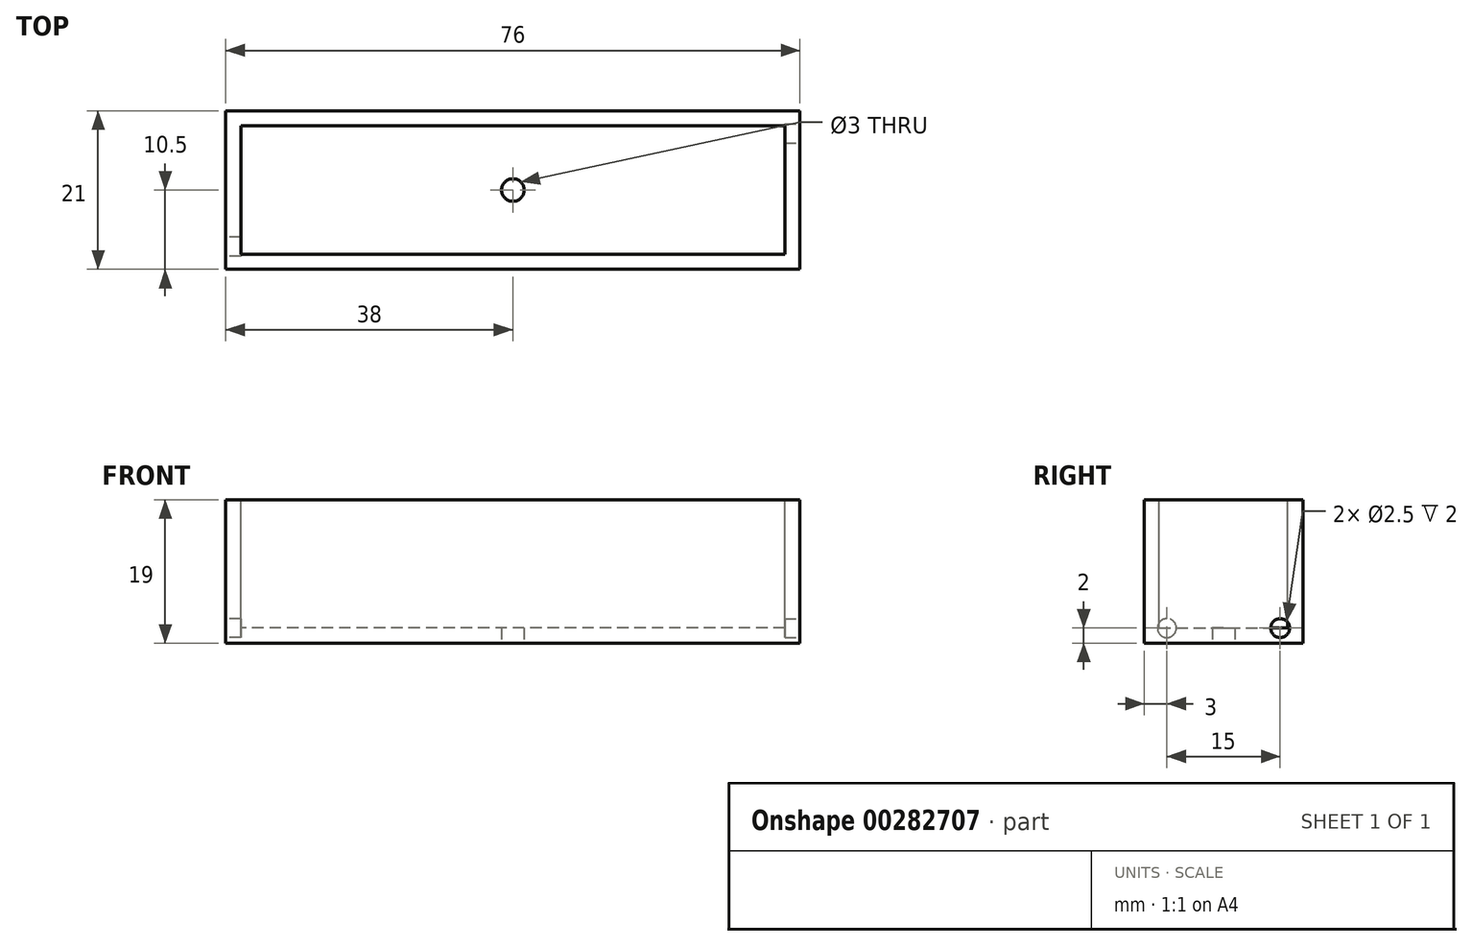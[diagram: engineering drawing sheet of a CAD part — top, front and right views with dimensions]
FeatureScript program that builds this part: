
annotation { "Feature Type Name" : "Feature", "Feature Type Description" : "" }
export const myFeature = defineFeature(function(context is Context, id is Id, definition is map)
    precondition{}
    {
        {
            var Q0;
            Q0=qCreatedBy(makeId("Top.planeOp"),FACE);
            var sketch = newSketch(context, id + "F0", { "sketchPlane" : qUnion([Q0])});
            skLineSegment(sketch, "E0.bottom", {"start": v(38, -10.5) * mm, "end": v(-38, -10.5) * mm});
            skLineSegment(sketch, "E0.top", {"start": v(38, 10.5) * mm, "end": v(-38, 10.5) * mm});
            skLineSegment(sketch, "E0.left", {"start": v(38, -10.5) * mm, "end": v(38, 10.5) * mm});
            skLineSegment(sketch, "E0.right", {"start": v(-38, -10.5) * mm, "end": v(-38, 10.5) * mm});
            skPoint(sketch, "E0.middle", {"position": v(0, 0) * mm});
            skSolve(sketch);
        }
        {
            var Q0;
            Q0=qSketchRegion(id+"F0",true);
            extrude(context, id + "F1", {"entities" : qUnion([Q0]), "depth" : 19 * mm});
        }
        {
            var Q0;
            Q0=makeQuery(id+"F1.opExtrude","CAP_FACE",FACE,{"disambiguationData":[OSD([sQuery(id+"F0.wireOp",EDGE,"E0.bottom"),sQuery(id+"F0.wireOp",EDGE,"E0.top"),sQuery(id+"F0.wireOp",EDGE,"E0.left"),sQuery(id+"F0.wireOp",EDGE,"E0.right")])],"isStart":false});
            var sketch = newSketch(context, id + "F2", { "sketchPlane" : qUnion([Q0])});
            skLineSegment(sketch, "E1.bottom", {"start": v(36, -8.5) * mm, "end": v(-36, -8.5) * mm});
            skLineSegment(sketch, "E1.top", {"start": v(36, 8.5) * mm, "end": v(-36, 8.5) * mm});
            skLineSegment(sketch, "E1.left", {"start": v(36, -8.5) * mm, "end": v(36, 8.5) * mm});
            skLineSegment(sketch, "E1.right", {"start": v(-36, -8.5) * mm, "end": v(-36, 8.5) * mm});
            skPoint(sketch, "E1.middle", {"position": v(0, 0) * mm});
            skSolve(sketch);
        }
        {
            var Q0;
            Q0=qSketchRegion(id+"F2",true);
            extrude(context, id + "F3", {"entities" : qUnion([Q0]), "operationType" : NewBodyOperationType.REMOVE, "oppositeDirection" : true, "depth" : 17 * mm});
        }
        {
            var Q0;
            Q0=makeQuery(id+"F1.opExtrude","CAP_FACE",FACE,{"disambiguationData":[OSD([sQuery(id+"F0.wireOp",EDGE,"E0.bottom"),sQuery(id+"F0.wireOp",EDGE,"E0.top"),sQuery(id+"F0.wireOp",EDGE,"E0.left"),sQuery(id+"F0.wireOp",EDGE,"E0.right")])],"isStart":true});
            var sketch = newSketch(context, id + "F4", { "sketchPlane" : qUnion([Q0])});
            skCircle(sketch, "E2", {"center": v(0, 0) * mm, "radius": 1.5 * mm});
            skSolve(sketch);
        }
        {
            var Q0;
            Q0=qSketchRegion(id+"F4",true);
            extrude(context, id + "F5", {"entities" : qUnion([Q0]), "operationType" : NewBodyOperationType.REMOVE, "endBound" : BoundingType.THROUGH_ALL, "oppositeDirection" : true, "depth" : 25 * mm});
        }
        {
            var Q0;
            Q0=makeQuery(id+"F1.opExtrude","SWEPT_FACE",FACE,{"disambiguationData":[OSD([sQuery(id+"F0.wireOp",EDGE,"E0.right")])]});
            var sketch = newSketch(context, id + "F6", { "sketchPlane" : qUnion([Q0])});
            skLineSegment(sketch, "E3.bottom", {"start": v(10.5, 0) * mm, "end": v(7.5, 0) * mm, "construction": true});
            skLineSegment(sketch, "E3.top", {"start": v(10.5, 2) * mm, "end": v(7.5, 2) * mm, "construction": true});
            skLineSegment(sketch, "E3.left", {"start": v(10.5, 0) * mm, "end": v(10.5, 2) * mm, "construction": true});
            skLineSegment(sketch, "E3.right", {"start": v(7.5, 0) * mm, "end": v(7.5, 2) * mm, "construction": true});
            skCircle(sketch, "E4", {"center": v(7.5, 2) * mm, "radius": 1.25 * mm});
            skPoint(sketch, "E5.centerSnap0", {"position": v(9, 0) * mm});
            skSolve(sketch);
        }
        {
            var Q0;
            Q0=qSketchRegion(id+"F6",true);
            extrude(context, id + "F7", {"entities" : qUnion([Q0]), "operationType" : NewBodyOperationType.REMOVE, "oppositeDirection" : true, "depth" : 2 * mm});
        }
        {
            var Q0;
            Q0=makeQuery(id+"F1.opExtrude","SWEPT_FACE",FACE,{"disambiguationData":[OSD([sQuery(id+"F0.wireOp",EDGE,"E0.left")])]});
            var sketch = newSketch(context, id + "F8", { "sketchPlane" : qUnion([Q0])});
            skLineSegment(sketch, "E6.bottom", {"start": v(10.5, 0) * mm, "end": v(7.5, 0) * mm, "construction": true});
            skLineSegment(sketch, "E6.top", {"start": v(10.5, 2) * mm, "end": v(7.5, 2) * mm});
            skLineSegment(sketch, "E6.left", {"start": v(10.5, 0) * mm, "end": v(10.5, 2) * mm, "construction": true});
            skLineSegment(sketch, "E6.right", {"start": v(7.5, 0) * mm, "end": v(7.5, 2) * mm});
            skCircle(sketch, "E7", {"center": v(7.5, 2) * mm, "radius": 1.25 * mm});
            skSolve(sketch);
        }
        {
            var Q0;
            Q0=qSketchRegion(id+"F8",true);
            extrude(context, id + "F9", {"entities" : qUnion([Q0]), "operationType" : NewBodyOperationType.REMOVE, "oppositeDirection" : true, "depth" : 2 * mm});
        }
    });
